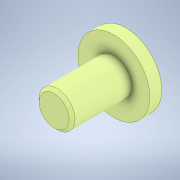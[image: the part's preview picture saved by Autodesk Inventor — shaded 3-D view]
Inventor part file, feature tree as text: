
AUTODESK INVENTOR PART (.ipt)
format: ipt  version: 2022 (Build 260153000, 153)  size: 108,544 bytes
history: native  units: in
note: dims shown in document units (in); Inventor stores cm internally (conversion verified against a paired STEP export)
features: extrude x2, sketch x2, chamfer x1
ambient origin geometry x8: Origin, YZ Plane, XZ Plane, XY Plane, X Axis, Y Axis, Z Axis, Center Point
bodies: Solid1 (feature_tree)
feature tree (5):
  extrude  "Extrusion1"  Depth=0.0787in TaperAngle=0.0deg
  extrude  "Extrusion2"  Depth=0.3937in TaperAngle=0.0deg
  chamfer  "Chamfer1"  Distance=0.0787in Angle=45.0deg
  sketch  "Sketch1"  dims[d0=0.4724in d1=0.0787in d2=0.0in]
  sketch  "Sketch2"  dims[d3=0.2362in d4=0.3937in d5=0.0in d6=0.0197in d7=0.0787in d8=45.0deg]
